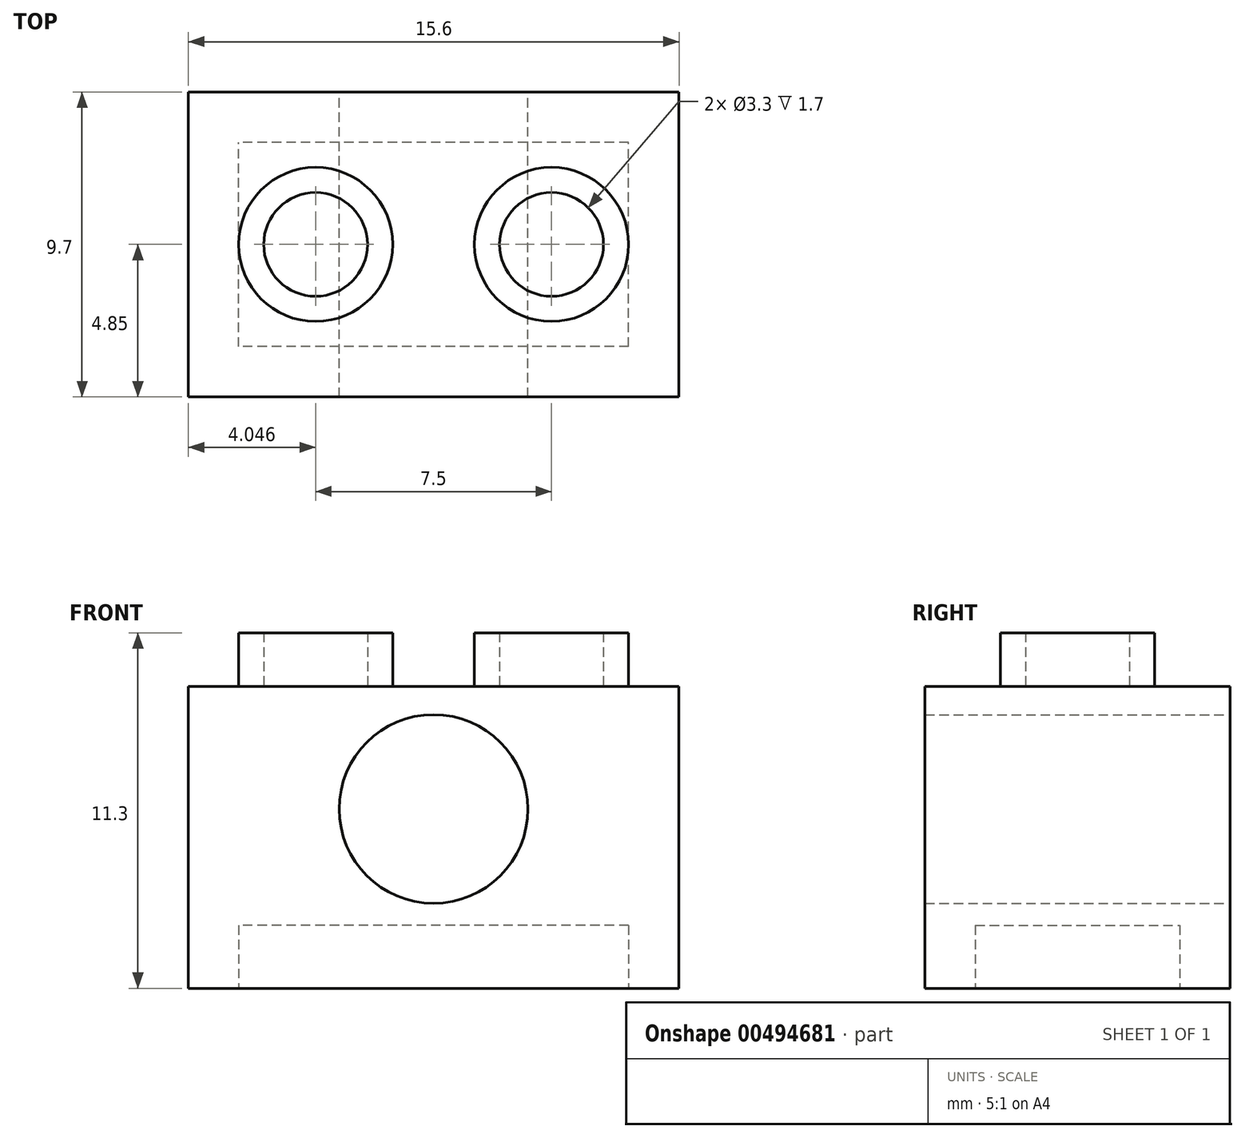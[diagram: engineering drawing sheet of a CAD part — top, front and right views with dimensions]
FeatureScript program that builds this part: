
annotation { "Feature Type Name" : "Feature", "Feature Type Description" : "" }
export const myFeature = defineFeature(function(context is Context, id is Id, definition is map)
    precondition{}
    {
        {
            var Q0;
            Q0=qCreatedBy(makeId("Front.planeOp"),FACE);
            var sketch = newSketch(context, id + "F0", { "sketchPlane" : qUnion([Q0])});
            skLineSegment(sketch, "E0", {"start": v(-13.16, 7.06) * mm, "end": v(-13.16, -2.54) * mm});
            skLineSegment(sketch, "E1", {"start": v(-13.16, -2.54) * mm, "end": v(2.44, -2.54) * mm});
            skLineSegment(sketch, "E2", {"start": v(2.44, -2.54) * mm, "end": v(2.44, 7.06) * mm});
            skLineSegment(sketch, "E3", {"start": v(-13.16, 7.06) * mm, "end": v(2.44, 7.06) * mm});
            skCircle(sketch, "E4", {"center": v(-5.36, 3.16) * mm, "radius": 3 * mm});
            skPoint(sketch, "E4.centerSnap0", {"position": v(-5.36, -2.54) * mm});
            skCircle(sketch, "E5", {"center": v(-5.36, 3.16) * mm, "radius": 2.3 * mm});
            skSolve(sketch);
        }
        {
            var Q0;
            Q0=makeQuery(id+"F0.imprint","IMPRINT",FACE,{"disambiguationData":[TD([[makeQuery(id+"F0.imprint","IMPRINT",EDGE,{"derivedFrom":sQuery(id+"F0.wireOp",EDGE,"E0")}),1.0]])]});
            extrude(context, id + "F1", {"entities" : qUnion([Q0]), "depth" : 19.7 * mm, "hasSecondDirection" : true, "secondDirectionOppositeDirection" : false, "secondDirectionDepth" : 10 * mm});
        }
        {
            var Q0;
            Q0=makeQuery(id+"F1.opExtrude","SWEPT_FACE",FACE,{"disambiguationData":[OSD([sQuery(id+"F0.wireOp",EDGE,"E3")])]});
            var sketch = newSketch(context, id + "F2", { "sketchPlane" : qUnion([Q0])});
            skCircle(sketch, "E6", {"center": v(-9.11, -14.85) * mm, "radius": 2.45 * mm});
            skPoint(sketch, "E6.centerSnap0", {"position": v(-13.16, -14.85) * mm});
            skCircle(sketch, "E7", {"center": v(-1.61, -14.85) * mm, "radius": 2.45 * mm});
            skPoint(sketch, "E7.centerSnap0", {"position": v(2.44, -14.85) * mm});
            skLineSegment(sketch, "E8", {"start": v(-5.36, -10) * mm, "end": v(-5.36, -19.7) * mm});
            skCircle(sketch, "E9", {"center": v(-9.11, -14.85) * mm, "radius": 1.65 * mm});
            skCircle(sketch, "E10", {"center": v(-1.61, -14.85) * mm, "radius": 1.65 * mm});
            skSolve(sketch);
        }
        {
            var Q0;
            Q0=makeQuery(id+"F2.imprint","IMPRINT",FACE,{"disambiguationData":[TD([[makeQuery(id+"F2.imprint","IMPRINT",EDGE,{"derivedFrom":sQuery(id+"F2.wireOp",EDGE,"E7")}),1.0]])]});
            var Q1;
            Q1=makeQuery(id+"F2.imprint","IMPRINT",FACE,{"disambiguationData":[TD([[makeQuery(id+"F2.imprint","IMPRINT",EDGE,{"derivedFrom":sQuery(id+"F2.wireOp",EDGE,"E6")}),1.0]])]});
            extrude(context, id + "F3", {"entities" : qUnion([Q0, Q1]), "operationType" : NewBodyOperationType.ADD, "depth" : 1.7 * mm});
        }
        {
            var Q0;
            Q0=makeQuery(id+"F1.opExtrude","SWEPT_FACE",FACE,{"disambiguationData":[OSD([sQuery(id+"F0.wireOp",EDGE,"E1")])]});
            var sketch = newSketch(context, id + "F4", { "sketchPlane" : qUnion([Q0])});
            skLineSegment(sketch, "E11", {"start": v(-13.16, 14.85) * mm, "end": v(-11.56, 14.85) * mm});
            skLineSegment(sketch, "E12", {"start": v(-5.36, 19.7) * mm, "end": v(-5.36, 18.1) * mm});
            skLineSegment(sketch, "E13.bottom", {"start": v(0.84, 18.1) * mm, "end": v(-11.56, 18.1) * mm});
            skLineSegment(sketch, "E13.top", {"start": v(0.84, 11.6) * mm, "end": v(-11.56, 11.6) * mm});
            skLineSegment(sketch, "E13.left", {"start": v(0.84, 18.1) * mm, "end": v(0.84, 11.6) * mm});
            skLineSegment(sketch, "E13.right", {"start": v(-11.56, 18.1) * mm, "end": v(-11.56, 11.6) * mm});
            skLineSegment(sketch, "E14.trimOffspring", {"start": v(0.84, 14.85) * mm, "end": v(2.44, 14.85) * mm});
            skLineSegment(sketch, "E15.trimOffspring", {"start": v(-5.36, 11.6) * mm, "end": v(-5.36, 10) * mm});
            skSolve(sketch);
        }
        {
            var Q0;
            {var subQ6=sQuery(id+"F4.wireOp",EDGE,"E13.bottom");var subQ7=makeQuery(id+"F4.imprint","INTERSECT",VERTEX,{"derivedFrom":[sQuery(id+"F4.wireOp",EDGE,"E12"),subQ6]});Q0=makeQuery(id+"F4.imprint","IMPRINT",FACE,{"disambiguationData":[TD([[makeQuery(id+"F4.imprint","IMPRINT",EDGE,{"disambiguationData":[TD([[subQ7,1.0]])],"derivedFrom":subQ6}),1.0]])]});}
            extrude(context, id + "F5", {"entities" : qUnion([Q0]), "operationType" : NewBodyOperationType.REMOVE, "oppositeDirection" : true, "depth" : 2 * mm});
        }
        {
            var Q0;
            Q0=makeQuery(id+"F0.imprint","IMPRINT",FACE,{"disambiguationData":[TD([[makeQuery(id+"F0.imprint","IMPRINT",EDGE,{"derivedFrom":sQuery(id+"F0.wireOp",EDGE,"E4")}),1.0]])]});
            extrude(context, id + "F6", {"entities" : qUnion([Q0]), "operationType" : NewBodyOperationType.REMOVE, "depth" : 0.8 * mm});
        }
        {
            var Q0;
            Q0=makeQuery(id+"F1.opExtrude","CAP_FACE",FACE,{"disambiguationData":[OSD([sQuery(id+"F0.wireOp",EDGE,"E0"),sQuery(id+"F0.wireOp",EDGE,"E1"),sQuery(id+"F0.wireOp",EDGE,"E2"),sQuery(id+"F0.wireOp",EDGE,"E3"),sQuery(id+"F0.wireOp",EDGE,"E5")])],"isStart":false});
            var sketch = newSketch(context, id + "F7", { "sketchPlane" : qUnion([Q0])});
            skLineSegment(sketch, "E16", {"start": v(-13.16, 7.06) * mm, "end": v(-13.16, -2.54) * mm});
            skLineSegment(sketch, "E17", {"start": v(-13.16, -2.54) * mm, "end": v(2.44, -2.54) * mm});
            skLineSegment(sketch, "E18", {"start": v(2.44, -2.54) * mm, "end": v(2.44, 7.06) * mm});
            skLineSegment(sketch, "E19", {"start": v(-13.16, 7.06) * mm, "end": v(2.44, 7.06) * mm});
            skCircle(sketch, "E20", {"center": v(-5.36, 3.16) * mm, "radius": 3 * mm});
            skPoint(sketch, "E20.centerSnap0", {"position": v(-5.36, -2.54) * mm});
            skCircle(sketch, "E21", {"center": v(-5.36, 3.16) * mm, "radius": 2.3 * mm});
            skSolve(sketch);
        }
        {
            var Q0;
            Q0=makeQuery(id+"F7.imprint","IMPRINT",FACE,{"disambiguationData":[TD([[makeQuery(id+"F7.imprint","IMPRINT",EDGE,{"derivedFrom":sQuery(id+"F7.wireOp",EDGE,"E20")}),1.0]])]});
            extrude(context, id + "F8", {"entities" : qUnion([Q0]), "operationType" : NewBodyOperationType.REMOVE, "oppositeDirection" : true, "depth" : 0.8 * mm});
        }
    });
